# Revit family: Storage-Teknion-CW3B_C+D_Three_Storage_Credenza_29_Height_Low_Base-R2020
name_source: partatom
category: Furniture
units: mm (PartAtom-declared; Revit-internal decimal feet)

## family parameters
Always vertical = Yes
Cut with Voids When Loaded = No
OmniClass Number = 23.40.20.00
OmniClass Title = General Furniture and Specialties
Room Calculation Point = No
Shared = Yes
Work Plane-Based = No

## types (4) — shared parameters
Assembly Code = E2020200
Manufacturer = Teknion
Manufacturer Fax = 416.661.4586
Part Number = CW3B
Product Documentation Link = https://www.teknion.com
Product Line = C+D Credenzas
Product Page URL = https://www.teknion.com
Series = C+D Conference Table
Sustainability Data = https://www.teknion.com
URL = www.teknion.com
Unit Weight URL = http://www.teknion.com
Warranty = http://www.teknion.com
zero-valued in all types: Default Elevation

## per-type parameters (varying)
| type | 20 2D Node | 24 2D Node | Depth | Description | Door C Size | Door L/R Size | Model | Width |
| 20D x 90W | Yes | No | 20 " | C+D Three Storage Credenza, 29" Height, Low Based, 20" Depth, 90" Width | 14.75 " | 14.75 " | CW3B_2090 | 90 " |
| 20D x 108W | Yes | No | 20 " | C+D Three Storage Credenza, 29" Height, Low Based, 20" Depth, 108" Width | 17.75 " | 17.769 " | CW3B_20108 | 108 " |
| 24D x 108W | No | Yes | 24 " | C+D Three Storage Credenza, 29" Height, Low Based, 24" Depth, 108" Width | 17.75 " | 17.769 " | CW3B_24108 | 108 " |
| 24D x 90W | No | Yes | 24 " | C+D Three Storage Credenza, 29" Height, Low Based, 24" Depth, 90" Width | 14.75 " | 14.75 " | CW3B_2490 | 90 " |

## geometry (parser evidence)
native form markers: Sweep x5
no freeform markers — native parametric forms only
